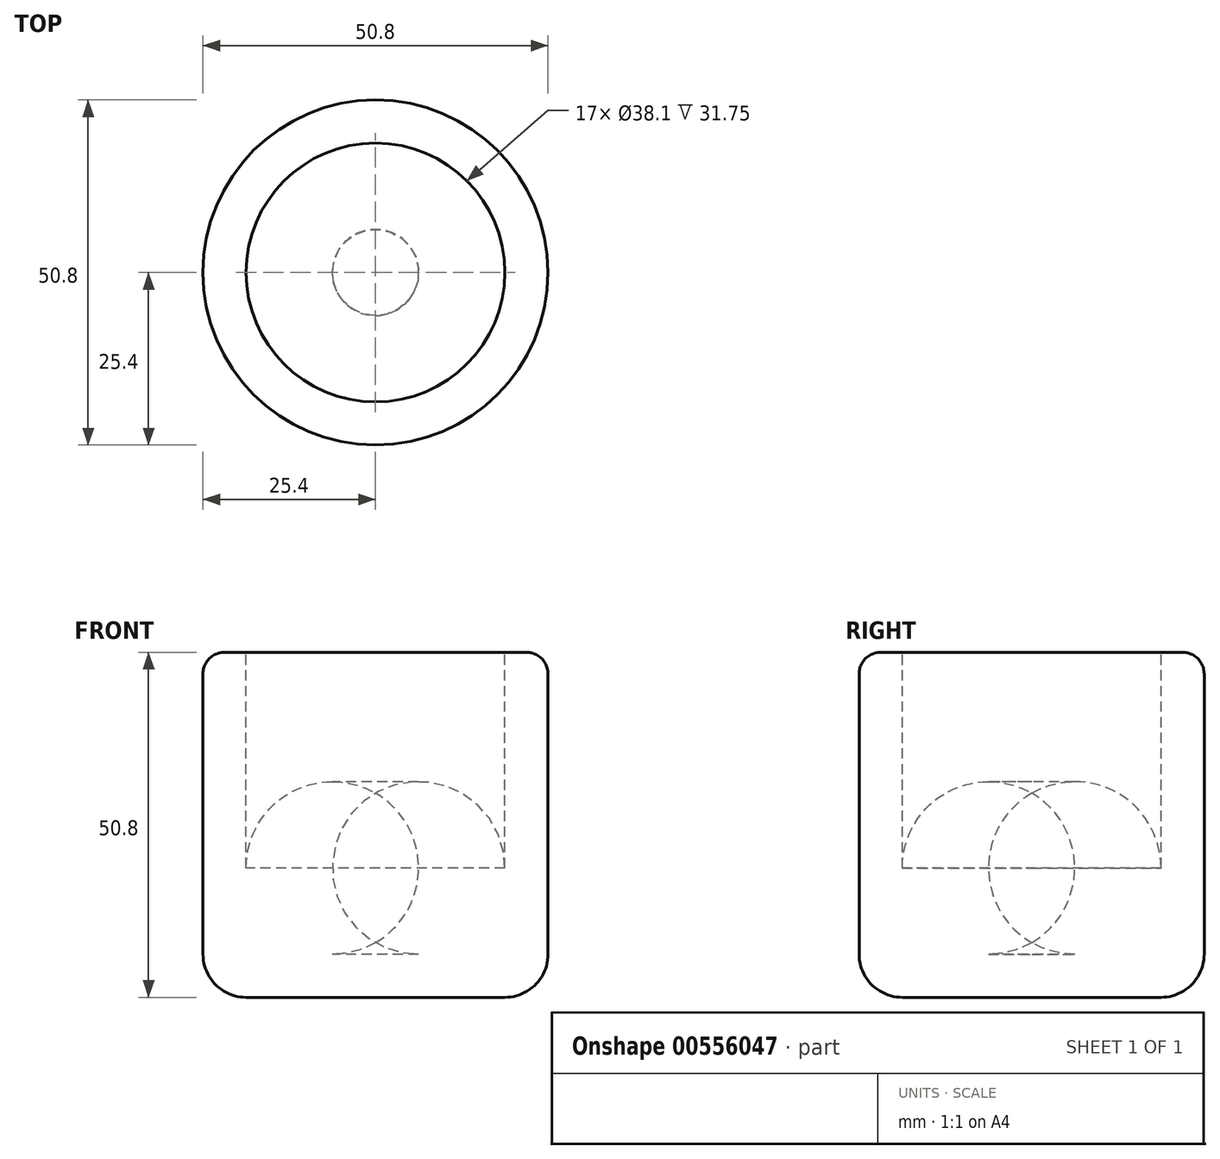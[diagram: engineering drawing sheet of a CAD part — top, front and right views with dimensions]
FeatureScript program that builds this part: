
annotation { "Feature Type Name" : "Feature", "Feature Type Description" : "" }
export const myFeature = defineFeature(function(context is Context, id is Id, definition is map)
    precondition{}
    {
        {
            var Q0;
            Q0=qCreatedBy(makeId("Top.planeOp"),FACE);
            var sketch = newSketch(context, id + "F0", { "sketchPlane" : qUnion([Q0])});
            skCircle(sketch, "E0", {"center": v(0, 0) * mm, "radius": 25.4 * mm});
            skSolve(sketch);
        }
        {
            var Q0;
            Q0 = qSketchRegion(id + "F0", true);
            extrude(context, id + "F1", {"entities" : qUnion([Q0]), "depth" : 50.8 * mm, "offsetDistance" : 25.4 * mm});
        }
        {
            var Q0;
            Q0=makeQuery(id+"F1.opExtrude","CAP_FACE",FACE,{"disambiguationData":[OSD([sQuery(id+"F0.wireOp",EDGE,"E0")])],"isStart":false});
            var sketch = newSketch(context, id + "F2", { "sketchPlane" : qUnion([Q0])});
            skCircle(sketch, "E1", {"center": v(0, 0) * mm, "radius": 19.05 * mm});
            skSolve(sketch);
        }
        {
            var Q0;
            Q0 = qSketchRegion(id + "F2", true);
            extrude(context, id + "F3", {"entities" : qUnion([Q0]), "operationType" : NewBodyOperationType.REMOVE, "oppositeDirection" : true, "depth" : 44.45 * mm, "offsetDistance" : 25.4 * mm});
        }
        {
            var Q0;
            Q0=makeQuery(id+"F1.opExtrude","CAP_EDGE",EDGE,{"disambiguationData":[OSD([sQuery(id+"F0.wireOp",EDGE,"E0")])],"isStart":false});
            var Q1;
            Q1=makeQuery(id+"F3.boolean.opBoolean","COPY",EDGE,{"derivedFrom":makeQuery(id+"F3.opExtrude","CAP_EDGE",EDGE,{"disambiguationData":[OSD([sQuery(id+"F2.wireOp",EDGE,"E1")])],"isStart":true})});
            fillet(context, id + "F4", {"entities" : qUnion([Q0, Q1]), "radius" : 3.17 * mm, "tangentPropagation" : true, "allowEdgeOverflow" : false});
        }
        {
            var Q0;
            Q0=makeQuery(id+"F3.boolean.opBoolean","COPY",EDGE,{"derivedFrom":makeQuery(id+"F3.opExtrude","CAP_EDGE",EDGE,{"disambiguationData":[OSD([sQuery(id+"F2.wireOp",EDGE,"E1")])],"isStart":false})});
            fillet(context, id + "F5", {"entities" : qUnion([Q0]), "radius" : 12.7 * mm, "tangentPropagation" : true, "allowEdgeOverflow" : false});
        }
        {
            var Q0;
            Q0=makeQuery(id+"F1.opExtrude","CAP_EDGE",EDGE,{"disambiguationData":[OSD([sQuery(id+"F0.wireOp",EDGE,"E0")])],"isStart":true});
            fillet(context, id + "F6", {"entities" : qUnion([Q0]), "radius" : 6.35 * mm, "tangentPropagation" : true, "allowEdgeOverflow" : false});
        }
    });
